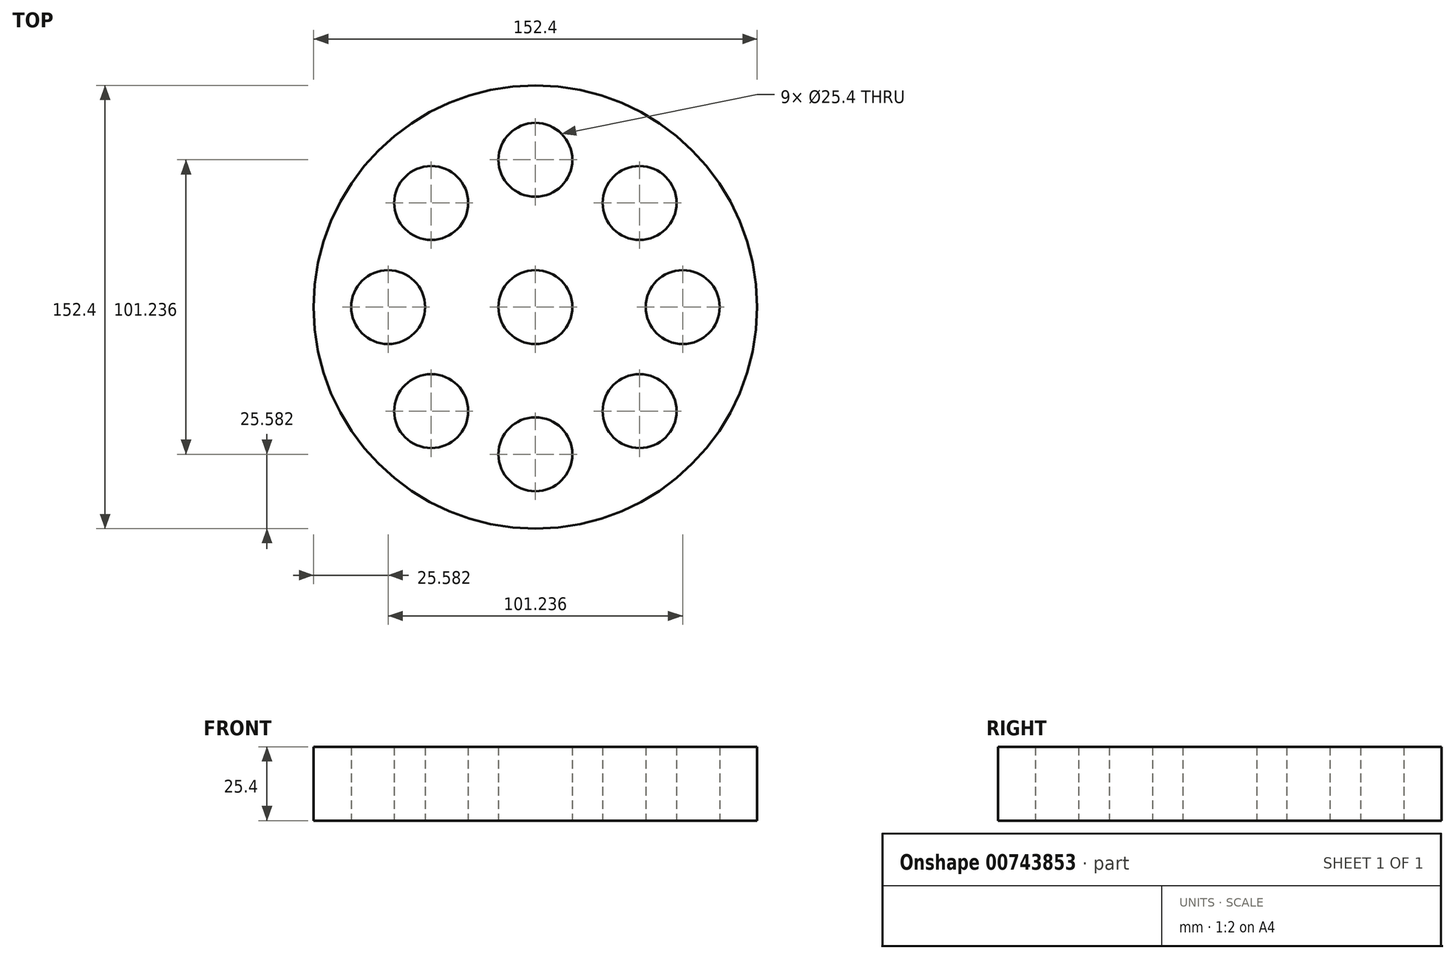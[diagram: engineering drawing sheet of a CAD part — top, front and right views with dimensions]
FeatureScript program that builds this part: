
annotation { "Feature Type Name" : "Feature", "Feature Type Description" : "" }
export const myFeature = defineFeature(function(context is Context, id is Id, definition is map)
    precondition{}
    {
        {
            var Q0;
            Q0=qCreatedBy(makeId("Top.planeOp"),FACE);
            var sketch = newSketch(context, id + "F0", { "sketchPlane" : qUnion([Q0])});
            skCircle(sketch, "E0", {"center": v(0, 0) * mm, "radius": 76.2 * mm});
            skCircle(sketch, "E1", {"center": v(0, 50.62) * mm, "radius": 12.7 * mm});
            skCircle(sketch, "E2.1.0", {"center": v(-35.8, 35.8) * mm, "radius": 12.7 * mm});
            skCircle(sketch, "E2.2.0", {"center": v(-50.62, 0) * mm, "radius": 12.7 * mm});
            skCircle(sketch, "E2.3.0", {"center": v(-35.8, -35.8) * mm, "radius": 12.7 * mm});
            skCircle(sketch, "E2.4.0", {"center": v(0, -50.62) * mm, "radius": 12.7 * mm});
            skCircle(sketch, "E2.5.0", {"center": v(35.8, -35.8) * mm, "radius": 12.7 * mm});
            skCircle(sketch, "E2.6.0", {"center": v(50.62, 0) * mm, "radius": 12.7 * mm});
            skCircle(sketch, "E2.7.0", {"center": v(35.8, 35.8) * mm, "radius": 12.7 * mm});
            skCircle(sketch, "E3", {"center": v(0, 0) * mm, "radius": 12.7 * mm});
            skSolve(sketch);
        }
        {
            var Q0;
            Q0=makeQuery(id+"F0.imprint","IMPRINT",FACE,{"disambiguationData":[TD([[makeQuery(id+"F0.imprint","IMPRINT",EDGE,{"derivedFrom":sQuery(id+"F0.wireOp",EDGE,"E0")}),1.0]])]});
            extrude(context, id + "F1", {"entities" : qUnion([Q0]), "depth" : 25.4 * mm, "offsetDistance" : 25.4 * mm});
        }
    });
